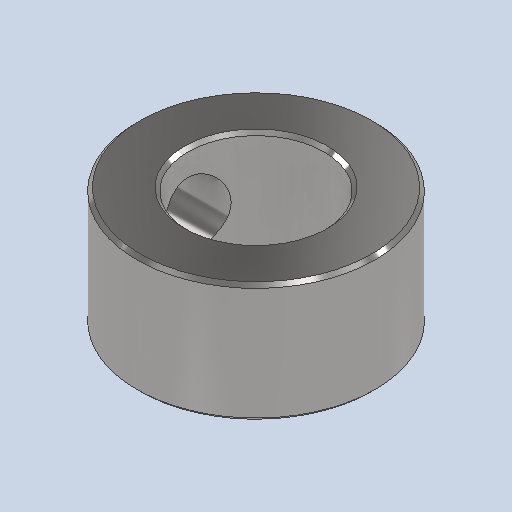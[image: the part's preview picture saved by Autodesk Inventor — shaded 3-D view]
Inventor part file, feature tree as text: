
AUTODESK INVENTOR PART (.ipt)
format: ipt  version: 2024 (Build 280153000, 153)  size: 149,504 bytes
history: native  units: mm
features: extrude x2, chamfer x1, sketch x1
ambient origin geometry x8: Origin, YZ Plane, XZ Plane, XY Plane, X Axis, Y Axis, Z Axis, Center Point
bodies: Solid1 (feature_tree)
feature tree (4):
  extrude  "Extrusion1"  Depth=3.5mm
  chamfer  "Chamfer1"  Distance=7.0mm
  extrude  "Extrusion2"  Depth=2.0mm TaperAngle=45.0deg
  sketch  "Sketch3"  dims[d0=14.0mm d1=8.0mm d2=7.0mm d3=0.0mm d4=0.2mm d5=2.0mm d6=45.0deg d7=4.0mm d8=3.5mm d9=7.0mm d10=0.0mm]
